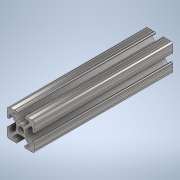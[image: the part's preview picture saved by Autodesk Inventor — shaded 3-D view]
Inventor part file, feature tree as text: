
AUTODESK INVENTOR PART (.ipt)
format: ipt  version: 2020 (Build 240168000, 168)  size: 240,640 bytes
history: native  units: in
note: dims shown in document units (in); Inventor stores cm internally (conversion verified against a paired STEP export)
features: extrude x1, sketch x1
ambient origin geometry x8: Origin, YZ Plane, XZ Plane, XY Plane, X Axis, Y Axis, Z Axis, Center Point
bodies: Solid1 (feature_tree)
feature tree (2):
  extrude  "Extrusion1"  [1 undecoded]
  sketch  "Sketch1"  dims[d0=5.0in d1=0.0in]
note: 1 required parameter value undecoded (feature->parameter linkage not recoverable at this tier; creation-order binding heuristic only, values carry confidence <= 0.55)
